# Revit family: P200921MX-044c_MGDB955F_CW
name_source: partatom
category: Specialty Equipment
units: mm (PartAtom-declared; Revit-internal decimal feet)

## family parameters
Always vertical = No
Cut with Voids When Loaded = No
Enable Cutting in Views = No
Maintain Annotation Orientation = No
Part Type = Normal
Room Calculation Point = No
Round Connector Dimension = Use Diameter
Shared = No
Work Plane-Based = No

## types (2) — shared parameters
Accent Material = ARCAT - Plastic - Gray
Amps = 0 A
Clearance Material = ARCAT - Clearance
Default Elevation = 0"
Depth = 33 1/2"
Description = Top Load Dryer with the PowerDry System and Extra Moisture Sensor – 9.2 cu. ft.
Sécheuse à chargement vertical à détecteur d'humidité, 9,2 pi3
Dimension Guide = http://whirlpool.com
http://whirlpool.com
Door Material = ARCAT - Metal - Steel - Stainless
Family Name = Laundry
Feature 1 = PowerDry system
PowerDry system
Feature 2 = PowerDry Cycle
Programme de séchage rapide PowerDry
Feature 3 = Magnetic Door Latch
Loquet de porte magnétique
Glass Material = ARCAT - Glass - Tempered - Black
Height = 43 7/16"
Installation-Fabrication = http://access.whirlpool.com Instruction&sku=MGDB955FW&language=EN
http://access.whirlpool.com Instruction&sku=MGDB955FW&language=FR
Knob Material = ARCAT - Metal - Steel - Stainless
Leg Material = ARCAT - Plastic - White
Manufacturer = Maytag
Voltage = 0 V
Width = 29"

## per-type parameters (varying)
| type | Body Material |
| MGDB955FC | ARCAT - Metal - Steel - Gray |
| MGDB955FW | ARCAT - Metal - Steel - White |

note: column(s) folded — value = type name in every type: Model

## geometry (parser evidence)
native form markers: Sweep x8
no freeform markers — native parametric forms only
